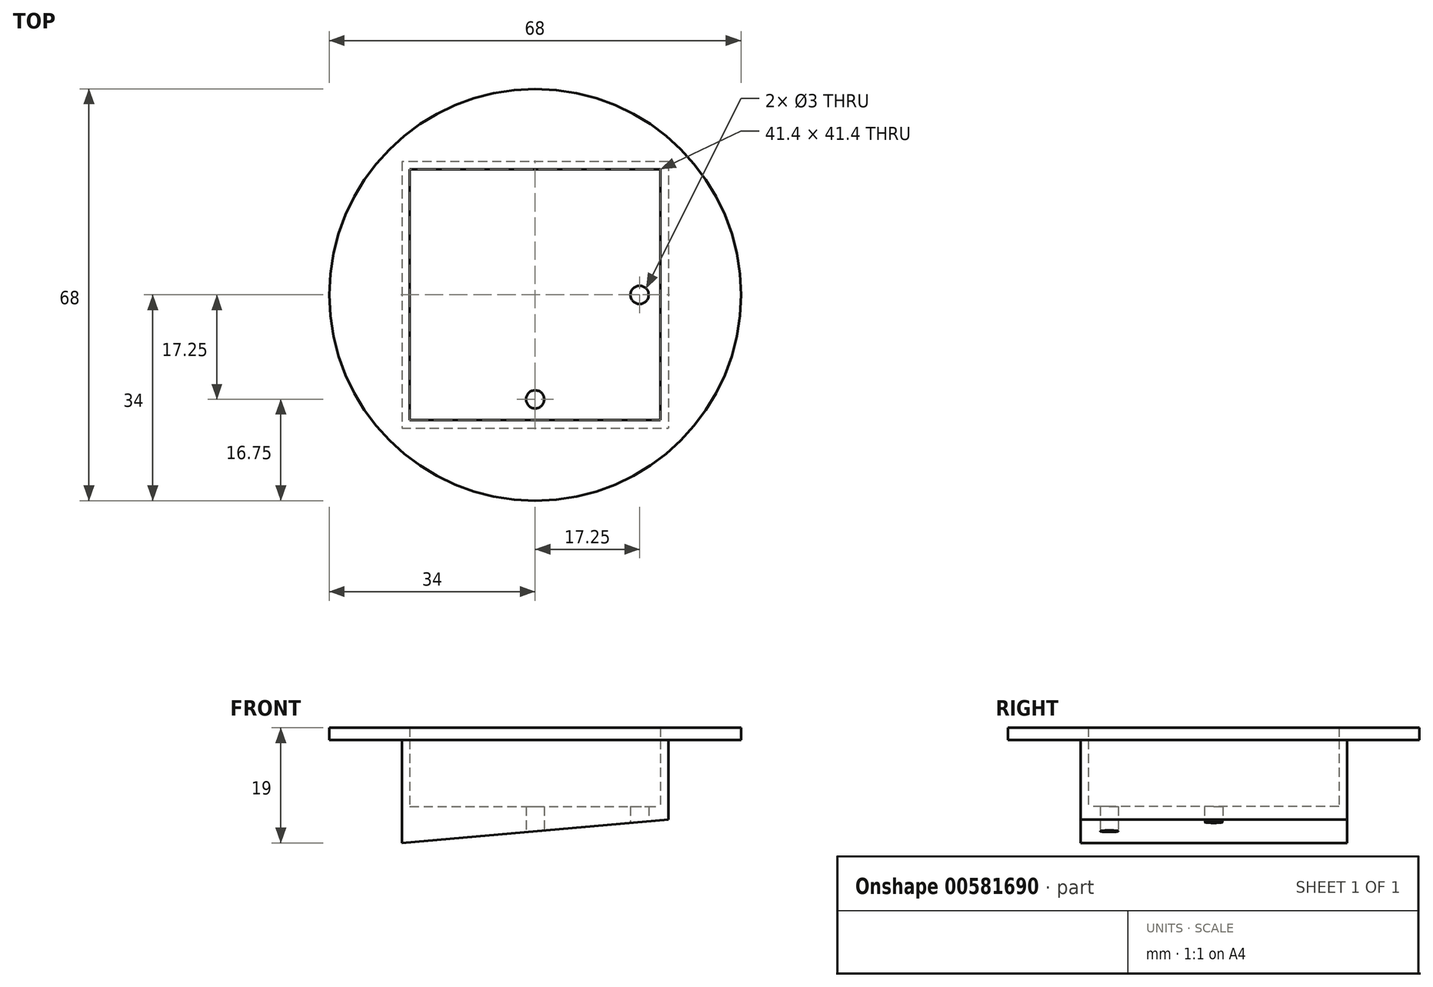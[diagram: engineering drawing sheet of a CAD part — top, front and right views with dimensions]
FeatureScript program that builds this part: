
annotation { "Feature Type Name" : "Feature", "Feature Type Description" : "" }
export const myFeature = defineFeature(function(context is Context, id is Id, definition is map)
    precondition{}
    {
        {
            var Q0;
            Q0=qCreatedBy(makeId("Top.planeOp"),FACE);
            var sketch = newSketch(context, id + "F0", { "sketchPlane" : qUnion([Q0])});
            skCircle(sketch, "E0", {"center": v(0, 0) * mm, "radius": 17.25 * mm, "construction": true});
            skLineSegment(sketch, "E1", {"start": v(0, 0) * mm, "end": v(0, 14.9) * mm, "construction": true});
            skLineSegment(sketch, "E2", {"start": v(0, 0) * mm, "end": v(12.33, 0) * mm, "construction": true});
            skCircle(sketch, "E3", {"center": v(0, 17.25) * mm, "radius": 1.5 * mm});
            skCircle(sketch, "E4.MirrorC", {"center": v(0, -17.25) * mm, "radius": 1.5 * mm});
            skLineSegment(sketch, "E5", {"start": v(0, 0) * mm, "end": v(10.4, 10.4) * mm, "construction": true});
            skCircle(sketch, "E6.MirrorC", {"center": v(17.25, 0) * mm, "radius": 1.5 * mm});
            skCircle(sketch, "E7.MirrorC", {"center": v(-17.25, 0) * mm, "radius": 1.5 * mm});
            skLineSegment(sketch, "E8.bottom", {"start": v(-22, 22) * mm, "end": v(22, 22) * mm});
            skLineSegment(sketch, "E8.top", {"start": v(-22, -22) * mm, "end": v(22, -22) * mm});
            skLineSegment(sketch, "E8.left", {"start": v(-22, 22) * mm, "end": v(-22, -22) * mm});
            skLineSegment(sketch, "E8.right", {"start": v(22, 22) * mm, "end": v(22, -22) * mm});
            skSolve(sketch);
        }
        {
            var Q0;
            Q0=makeQuery(id+"F0.imprint","IMPRINT",FACE,{"disambiguationData":[TD([[makeQuery(id+"F0.imprint","IMPRINT",EDGE,{"derivedFrom":sQuery(id+"F0.wireOp",EDGE,"E3")}),-1.0]])]});
            var Q1;
            Q1=makeQuery(id+"F0.imprint","IMPRINT",FACE,{"disambiguationData":[TD([[makeQuery(id+"F0.imprint","IMPRINT",EDGE,{"derivedFrom":sQuery(id+"F0.wireOp",EDGE,"E4.MirrorC")}),-1.0]])]});
            var Q2;
            Q2=makeQuery(id+"F0.imprint","IMPRINT",FACE,{"disambiguationData":[TD([[makeQuery(id+"F0.imprint","IMPRINT",EDGE,{"derivedFrom":sQuery(id+"F0.wireOp",EDGE,"E7.MirrorC")}),1.0]])]});
            var Q3;
            Q3=makeQuery(id+"F0.imprint","IMPRINT",FACE,{"disambiguationData":[TD([[makeQuery(id+"F0.imprint","IMPRINT",EDGE,{"derivedFrom":sQuery(id+"F0.wireOp",EDGE,"E6.MirrorC")}),-1.0]])]});
            var Q4;
            Q4=makeQuery(id+"F0.imprint","IMPRINT",FACE,{"disambiguationData":[TD([[makeQuery(id+"F0.imprint","IMPRINT",EDGE,{"derivedFrom":sQuery(id+"F0.wireOp",EDGE,"E3")}),1.0]])]});
            extrude(context, id + "F1", {"entities" : qUnion([Q0, Q1, Q2, Q3, Q4]), "depth" : 6 * mm, "offsetDistance" : 25 * mm});
        }
        {
            var Q0;
            Q0=makeQuery(id+"F1.opExtrude","CAP_FACE",FACE,{"disambiguationData":[OSD([sQuery(id+"F0.wireOp",EDGE,"E3"),sQuery(id+"F0.wireOp",EDGE,"E4.MirrorC"),sQuery(id+"F0.wireOp",EDGE,"E6.MirrorC"),sQuery(id+"F0.wireOp",EDGE,"E7.MirrorC"),sQuery(id+"F0.wireOp",EDGE,"E8.bottom"),sQuery(id+"F0.wireOp",EDGE,"E8.top"),sQuery(id+"F0.wireOp",EDGE,"E8.left"),sQuery(id+"F0.wireOp",EDGE,"E8.right")])],"isStart":false});
            var sketch = newSketch(context, id + "F2", { "sketchPlane" : qUnion([Q0])});
            skLineSegment(sketch, "E9.0", {"start": v(-20.7, 20.7) * mm, "end": v(20.7, 20.7) * mm});
            skLineSegment(sketch, "E9.1", {"start": v(-20.7, 20.7) * mm, "end": v(-20.7, -20.7) * mm});
            skLineSegment(sketch, "E9.2", {"start": v(-20.7, -20.7) * mm, "end": v(20.7, -20.7) * mm});
            skLineSegment(sketch, "E9.3", {"start": v(20.7, 20.7) * mm, "end": v(20.7, -20.7) * mm});
            skSolve(sketch);
        }
        {
            var Q0;
            Q0=makeQuery(id+"F2.imprint","IMPRINT",FACE,{"disambiguationData":[TD([[makeQuery(id+"F2.imprint","IMPRINT",EDGE,{"derivedFrom":sQuery(id+"F2.wireOp",EDGE,"E9.0")}),1.0]])]});
            extrude(context, id + "F3", {"entities" : qUnion([Q0]), "operationType" : NewBodyOperationType.ADD, "depth" : 11 * mm, "offsetDistance" : 25 * mm});
        }
        {
            var Q0;
            Q0=makeQuery(id+"F3.opExtrude","CAP_FACE",FACE,{"disambiguationData":[OSD([sQuery(id+"F0.wireOp",EDGE,"E8.bottom"),sQuery(id+"F0.wireOp",EDGE,"E8.top"),sQuery(id+"F0.wireOp",EDGE,"E8.left"),sQuery(id+"F0.wireOp",EDGE,"E8.right"),sQuery(id+"F2.wireOp",EDGE,"E9.0"),sQuery(id+"F2.wireOp",EDGE,"E9.1"),sQuery(id+"F2.wireOp",EDGE,"E9.2"),sQuery(id+"F2.wireOp",EDGE,"E9.3")])],"isStart":false});
            var sketch = newSketch(context, id + "F4", { "sketchPlane" : qUnion([Q0])});
            skLineSegment(sketch, "E10", {"start": v(-22, 22) * mm, "end": v(22, -22) * mm});
            skLineSegment(sketch, "E11", {"start": v(24.04, 24.04) * mm, "end": v(-22, -22) * mm});
            skCircle(sketch, "E12", {"center": v(0, 0) * mm, "radius": 34 * mm});
            skLineSegment(sketch, "E13.bottom", {"start": v(-20.7, 20.7) * mm, "end": v(20.7, 20.7) * mm});
            skLineSegment(sketch, "E13.top", {"start": v(-20.7, -20.7) * mm, "end": v(20.7, -20.7) * mm});
            skLineSegment(sketch, "E13.left", {"start": v(-20.7, 20.7) * mm, "end": v(-20.7, -20.7) * mm});
            skLineSegment(sketch, "E13.right", {"start": v(20.7, 20.7) * mm, "end": v(20.7, -20.7) * mm});
            skSolve(sketch);
        }
        {
            var Q0;
            Q0=makeQuery(id+"F4.imprint","IMPRINT",FACE,{"disambiguationData":[TD([[makeQuery(id+"F4.imprint","IMPRINT",EDGE,{"derivedFrom":sQuery(id+"F4.wireOp",EDGE,"E12")}),1.0]])]});
            var Q1;
            {var subQ2=sQuery(id+"F4.wireOp",EDGE,"E13.bottom");Q1=makeQuery(id+"F4.imprint","IMPRINT",FACE,{"disambiguationData":[TD([[makeQuery(id+"F4.imprint","IMPRINT",EDGE,{"derivedFrom":subQ2}),1.0]])]});}
            var Q2;
            {var subQ2=sQuery(id+"F4.wireOp",EDGE,"E13.right");Q2=makeQuery(id+"F4.imprint","IMPRINT",FACE,{"disambiguationData":[TD([[makeQuery(id+"F4.imprint","IMPRINT",EDGE,{"derivedFrom":subQ2}),1.0]])]});}
            var Q3;
            {var subQ2=sQuery(id+"F4.wireOp",EDGE,"E13.left");Q3=makeQuery(id+"F4.imprint","IMPRINT",FACE,{"disambiguationData":[TD([[makeQuery(id+"F4.imprint","IMPRINT",EDGE,{"derivedFrom":subQ2}),-1.0]])]});}
            var Q4;
            {var subQ2=sQuery(id+"F4.wireOp",EDGE,"E13.top");Q4=makeQuery(id+"F4.imprint","IMPRINT",FACE,{"disambiguationData":[TD([[makeQuery(id+"F4.imprint","IMPRINT",EDGE,{"derivedFrom":subQ2}),-1.0]])]});}
            extrude(context, id + "F5", {"entities" : qUnion([Q0, Q1, Q2, Q3, Q4]), "depth" : 2 * mm, "offsetDistance" : 25 * mm});
        }
        {
            var Q0;
            {var subQ0=sQuery(id+"F0.wireOp",EDGE,"E8.top");Q0=makeQuery(id+"F3.boolean.opBoolean","MERGE",FACE,{"derivedFrom":[makeQuery(id+"F1.opExtrude","SWEPT_FACE",FACE,{"disambiguationData":[OSD([subQ0])]}),makeQuery(id+"F3.opExtrude","SWEPT_FACE",FACE,{"disambiguationData":[OSD([subQ0])]})]});}
            var sketch = newSketch(context, id + "F6", { "sketchPlane" : qUnion([Q0])});
            skLineSegment(sketch, "E14", {"start": v(22, 0) * mm, "end": v(-22, 0) * mm});
            skLineSegment(sketch, "E15", {"start": v(-22, 0) * mm, "end": v(22, 3.85) * mm});
            skSolve(sketch);
        }
        {
            var Q0;
            {var subQ0=sQuery(id+"F6.wireOp",EDGE,"E14");Q0=makeQuery(id+"F6.imprint","IMPRINT",FACE,{"disambiguationData":[TD([[makeQuery(id+"F6.imprint","IMPRINT",EDGE,{"derivedFrom":subQ0}),1.0]])]});}
            extrude(context, id + "F7", {"entities" : qUnion([Q0]), "operationType" : NewBodyOperationType.REMOVE, "endBound" : BoundingType.THROUGH_ALL, "oppositeDirection" : true, "depth" : 25 * mm, "offsetDistance" : 25 * mm});
        }
        {
            var Q0;
            Q0=makeQuery(id+"F7.boolean.opBoolean","COPY",FACE,{"derivedFrom":makeQuery(id+"F7.opExtrude","SWEPT_FACE",FACE,{"disambiguationData":[OSD([sQuery(id+"F6.wireOp",EDGE,"E15")])]})});
            var sketch = newSketch(context, id + "F8", { "sketchPlane" : qUnion([Q0])});
            skLineSegment(sketch, "E16.bottom", {"start": v(-21.92, 22) * mm, "end": v(22.25, 22) * mm});
            skLineSegment(sketch, "E16.top", {"start": v(-21.92, -22) * mm, "end": v(22.25, -22) * mm});
            skLineSegment(sketch, "E16.left", {"start": v(-21.92, 22) * mm, "end": v(-21.92, -22) * mm});
            skLineSegment(sketch, "E16.right", {"start": v(22.25, 22) * mm, "end": v(22.25, -22) * mm});
            skSolve(sketch);
        }
        {
            var Q0;
            Q0=makeQuery(id+"F5.opExtrude","CAP_FACE",FACE,{"disambiguationData":[OSD([sQuery(id+"F4.wireOp",EDGE,"E12"),sQuery(id+"F4.wireOp",EDGE,"E13.bottom"),sQuery(id+"F4.wireOp",EDGE,"E13.top"),sQuery(id+"F4.wireOp",EDGE,"E13.left"),sQuery(id+"F4.wireOp",EDGE,"E13.right")])],"isStart":true});
            var sketch = newSketch(context, id + "F9", { "sketchPlane" : qUnion([Q0])});
            skCircle(sketch, "E17", {"center": v(0, 0) * mm, "radius": 34 * mm});
            skPoint(sketch, "E17.first.point", {"position": v(-24.1, 23.97) * mm});
            skPoint(sketch, "E17.second.point", {"position": v(-27.37, -20.18) * mm});
            skPoint(sketch, "E17.third.point", {"position": v(33.8, 3.62) * mm});
            skSolve(sketch);
        }
        {
            var Q0;
            Q0 = qSketchRegion(id + "F8", true);
            var Q1;
            Q1 = qSketchRegion(id + "F9", true);
            var Q2;
            Q2 = qConstructionFilter(qBodyType(qCreatedBy(id + "F8" ,EDGE), BodyType.WIRE), ConstructionObject.NO);
            var Q3;
            Q3 = qConstructionFilter(qBodyType(qCreatedBy(id + "F9" ,EDGE), BodyType.WIRE), ConstructionObject.NO);
            loft(context, id + "F10", {"bodyType" : ToolBodyType.SURFACE, "sheetProfilesArray" : [{ "sheetProfileEntities" : qUnion([Q0]) }, { "sheetProfileEntities" : qUnion([Q1]) }], "wireProfilesArray" : [{ "wireProfileEntities" : qUnion([Q2]) }, { "wireProfileEntities" : qUnion([Q3]) }]});
        }
    });
